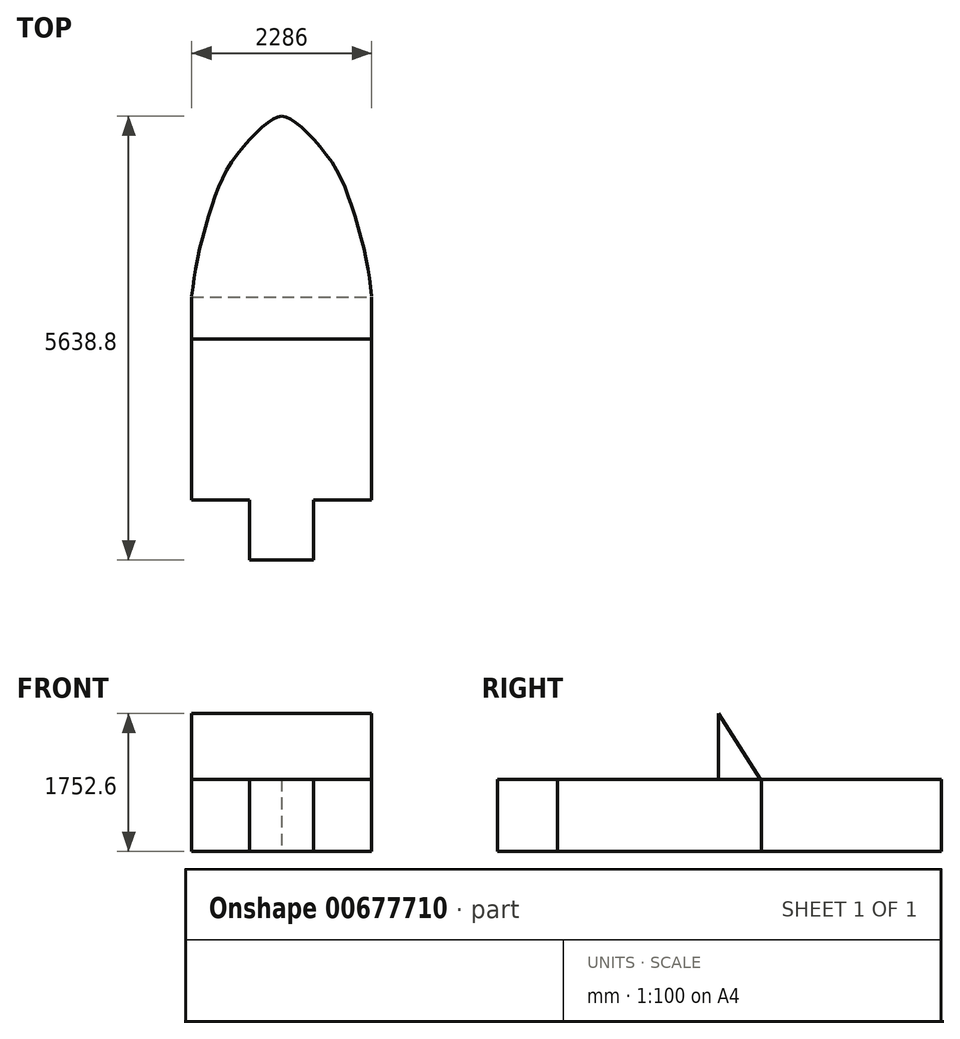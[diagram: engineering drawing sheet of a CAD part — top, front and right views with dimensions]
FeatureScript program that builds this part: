
annotation { "Feature Type Name" : "Feature", "Feature Type Description" : "" }
export const myFeature = defineFeature(function(context is Context, id is Id, definition is map)
    precondition{}
    {
        {
            var Q0;
            Q0=qCreatedBy(makeId("Top.planeOp"),FACE);
            var sketch = newSketch(context, id + "F0", { "sketchPlane" : qUnion([Q0])});
            skLineSegment(sketch, "E0", {"start": v(0, 0) * mm, "end": v(0, 2286) * mm, "construction": true});
            skLineSegment(sketch, "E1", {"start": v(0, 0) * mm, "end": v(1143, 0) * mm, "construction": true});
            skFitSpline(sketch, "E2", {"points": [v(0, 2286) * mm, v(114.94, 2245.45) * mm, v(364.66, 2035.02) * mm, v(678.9, 1630.98) * mm, v(883.34, 1156.41) * mm, v(1067.38, 491.07) * mm, v(1143, 0) * mm], "startDerivative": vector(1202.94, -285.8) * mm, "endDerivative": vector(313.4, -2575.29) * mm});
            skFitSpline(sketch, "E3.MirrorCS", {"points": [v(0, 2286) * mm, v(-114.94, 2245.45) * mm, v(-364.66, 2035.02) * mm, v(-678.9, 1630.98) * mm, v(-883.34, 1156.41) * mm, v(-1067.38, 491.07) * mm, v(-1143, 0) * mm], "startDerivative": vector(-1202.94, -285.8) * mm, "endDerivative": vector(-313.4, -2575.29) * mm});
            skLineSegment(sketch, "E4", {"start": v(-1143, 0) * mm, "end": v(-1143, -2590.8) * mm});
            skLineSegment(sketch, "E5", {"start": v(-406.4, -3352.8) * mm, "end": v(406.4, -3352.8) * mm});
            skLineSegment(sketch, "E6", {"start": v(1143, -2590.8) * mm, "end": v(1143, 0) * mm});
            skLineSegment(sketch, "E7", {"start": v(0, 0) * mm, "end": v(0, -4057.28) * mm, "construction": true});
            skPoint(sketch, "E8.middle", {"position": v(0, -4057.28) * mm});
            skLineSegment(sketch, "E9", {"start": v(-1143, -2590.8) * mm, "end": v(1143, -2590.8) * mm});
            skLineSegment(sketch, "E10", {"start": v(-406.4, -2590.8) * mm, "end": v(-406.4, -3352.8) * mm});
            skLineSegment(sketch, "E11", {"start": v(406.4, -2590.8) * mm, "end": v(406.4, -3352.8) * mm});
            skSolve(sketch);
        }
        {
            var Q0;
            Q0 = qSketchRegion(id + "F0", true);
            extrude(context, id + "F1", {"entities" : qUnion([Q0]), "depth" : 914.4 * mm, "offsetDistance" : 25.4 * mm});
        }
        {
            var Q0;
            Q0=makeQuery(id+"F1.opExtrude","SWEPT_FACE",FACE,{"disambiguationData":[OSD([sQuery(id+"F0.wireOp",EDGE,"E6")])]});
            var sketch = newSketch(context, id + "F2", { "sketchPlane" : qUnion([Q0])});
            skLineSegment(sketch, "E12", {"start": v(-15.32, 913.81) * mm, "end": v(-548.72, 1752.6) * mm});
            skLineSegment(sketch, "E13", {"start": v(-548.72, 1752.6) * mm, "end": v(-548.72, 914.4) * mm});
            skLineSegment(sketch, "E14", {"start": v(-548.72, 914.4) * mm, "end": v(-15.32, 913.81) * mm});
            skSolve(sketch);
        }
        {
            var Q0;
            Q0 = qSketchRegion(id + "F2", true);
            extrude(context, id + "F3", {"entities" : qUnion([Q0]), "oppositeDirection" : true, "depth" : 2286 * mm, "offsetDistance" : 25.4 * mm});
        }
    });
